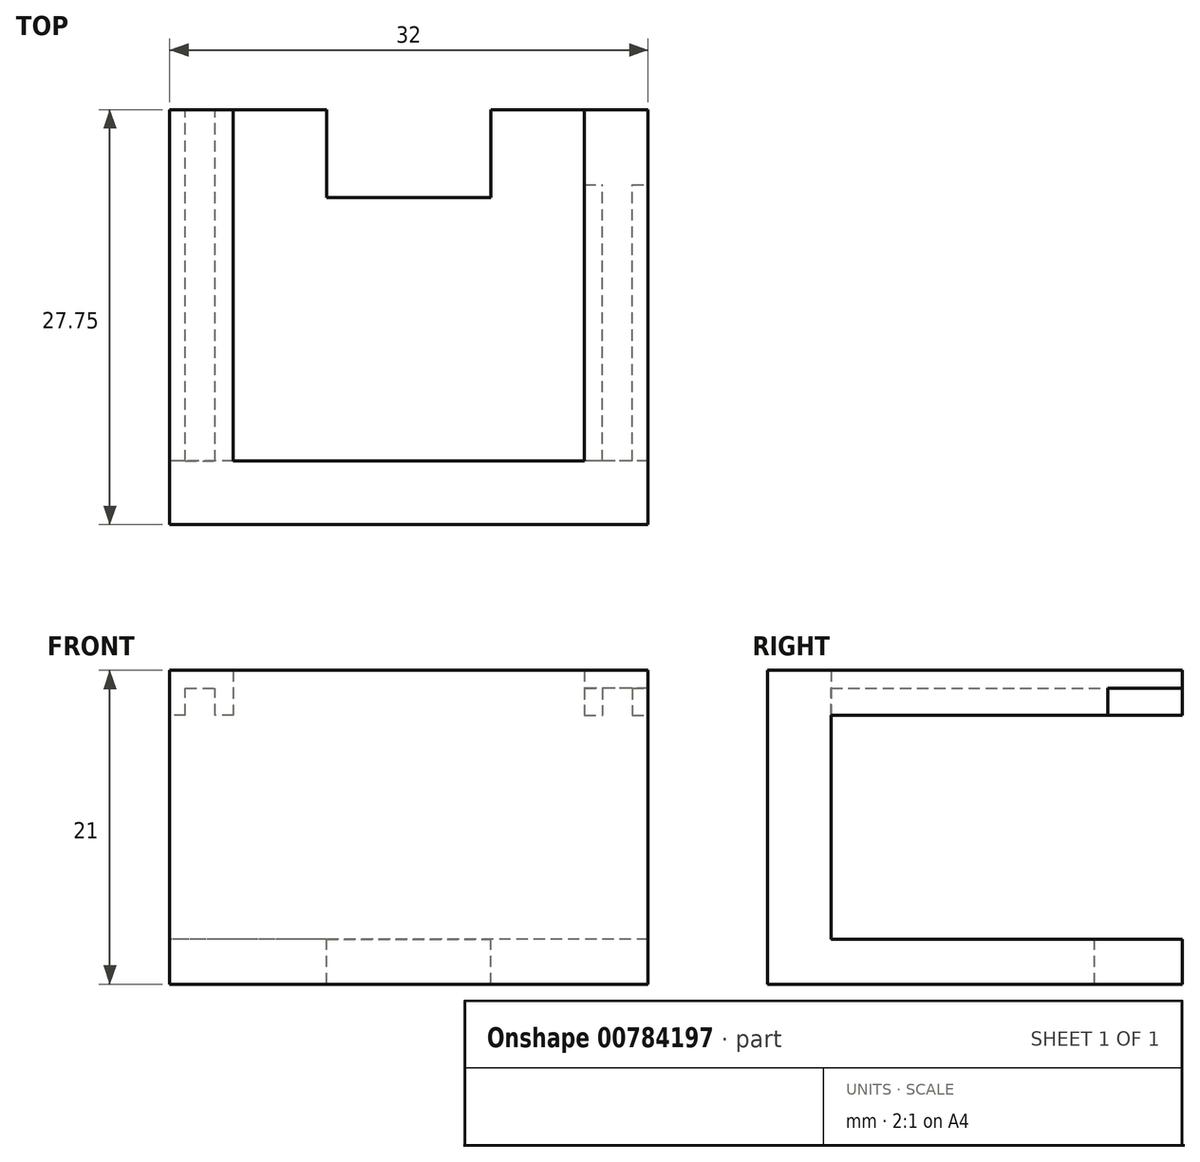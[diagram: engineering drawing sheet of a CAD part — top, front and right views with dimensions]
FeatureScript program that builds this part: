
annotation { "Feature Type Name" : "Feature", "Feature Type Description" : "" }
export const myFeature = defineFeature(function(context is Context, id is Id, definition is map)
    precondition{}
    {
        {
            var Q0;
            Q0=qCreatedBy(makeId("Top.planeOp"),FACE);
            var sketch = newSketch(context, id + "F0", { "sketchPlane" : qUnion([Q0])});
            skLineSegment(sketch, "E0.bottom", {"start": v(11.75, -11.75) * mm, "end": v(-11.75, -11.75) * mm});
            skLineSegment(sketch, "E0.left", {"start": v(11.75, -11.75) * mm, "end": v(11.75, 11.75) * mm});
            skLineSegment(sketch, "E0.right", {"start": v(-11.75, -11.75) * mm, "end": v(-11.75, 11.75) * mm});
            skPoint(sketch, "E0.middle", {"position": v(0, 0) * mm});
            skLineSegment(sketch, "E1", {"start": v(-16, 11.75) * mm, "end": v(-16, -16) * mm});
            skLineSegment(sketch, "E2", {"start": v(-16, -16) * mm, "end": v(16, -16) * mm});
            skLineSegment(sketch, "E3", {"start": v(16, -16) * mm, "end": v(16, 11.75) * mm});
            skPoint(sketch, "E4", {"position": v(0, -16) * mm});
            skLineSegment(sketch, "E5", {"start": v(-11.75, 11.75) * mm, "end": v(-16, 11.75) * mm});
            skLineSegment(sketch, "E6", {"start": v(11.75, 11.75) * mm, "end": v(16, 11.75) * mm});
            skSolve(sketch);
        }
        {
            var Q0;
            Q0 = qSketchRegion(id + "F0", true);
            extrude(context, id + "F1", {"entities" : qUnion([Q0]), "depth" : 3 * mm, "offsetDistance" : 25 * mm});
        }
        {
            var Q0;
            Q0=makeQuery(id+"F1.opExtrude","CAP_FACE",FACE,{"disambiguationData":[OSD([sQuery(id+"F0.wireOp",EDGE,"E0.bottom"),sQuery(id+"F0.wireOp",EDGE,"E0.left"),sQuery(id+"F0.wireOp",EDGE,"E0.right"),sQuery(id+"F0.wireOp",EDGE,"E1"),sQuery(id+"F0.wireOp",EDGE,"E2"),sQuery(id+"F0.wireOp",EDGE,"E3"),sQuery(id+"F0.wireOp",EDGE,"E5"),sQuery(id+"F0.wireOp",EDGE,"E6")])],"isStart":true});
            var sketch = newSketch(context, id + "F2", { "sketchPlane" : qUnion([Q0])});
            skLineSegment(sketch, "E7.bottom", {"start": v(-16, 16) * mm, "end": v(16, 16) * mm});
            skLineSegment(sketch, "E7.top", {"start": v(-16, 11.75) * mm, "end": v(16, 11.75) * mm});
            skLineSegment(sketch, "E7.left", {"start": v(-16, 16) * mm, "end": v(-16, 11.75) * mm});
            skLineSegment(sketch, "E7.right", {"start": v(16, 16) * mm, "end": v(16, 11.75) * mm});
            skSolve(sketch);
        }
        {
            var Q0;
            Q0 = qSketchRegion(id + "F2", true);
            extrude(context, id + "F3", {"entities" : qUnion([Q0]), "operationType" : NewBodyOperationType.ADD, "depth" : 15 * mm, "offsetDistance" : 25 * mm});
        }
        {
            var Q0;
            Q0=makeQuery(id+"F3.boolean.opBoolean","MERGE",FACE,{"derivedFrom":[makeQuery(id+"F1.opExtrude","SWEPT_FACE",FACE,{"disambiguationData":[OSD([sQuery(id+"F0.wireOp",EDGE,"E2")])]}),makeQuery(id+"F3.opExtrude","SWEPT_FACE",FACE,{"disambiguationData":[OSD([sQuery(id+"F2.wireOp",EDGE,"E7.bottom")])]})]});
            var sketch = newSketch(context, id + "F4", { "sketchPlane" : qUnion([Q0])});
            skLineSegment(sketch, "E8.bottom", {"start": v(-16, -15) * mm, "end": v(16, -15) * mm});
            skLineSegment(sketch, "E8.top", {"start": v(-16, -18) * mm, "end": v(16, -18) * mm});
            skLineSegment(sketch, "E8.left", {"start": v(-16, -15) * mm, "end": v(-16, -18) * mm});
            skLineSegment(sketch, "E8.right", {"start": v(16, -15) * mm, "end": v(16, -18) * mm});
            skSolve(sketch);
        }
        {
            var Q0;
            Q0 = qSketchRegion(id + "F4", true);
            var Q1;
            Q1=makeQuery(id+"F1.opExtrude","SWEPT_FACE",FACE,{"disambiguationData":[OSD([sQuery(id+"F0.wireOp",EDGE,"E5")])]});
            extrude(context, id + "F5", {"entities" : qUnion([Q0]), "operationType" : NewBodyOperationType.ADD, "endBound" : BoundingType.UP_TO_SURFACE, "oppositeDirection" : true, "depth" : 25 * mm, "endBoundEntityFace" : qUnion([Q1]), "offsetDistance" : 25 * mm});
        }
        {
            var Q0;
            Q0=makeQuery(id+"F1.opExtrude","SWEPT_FACE",FACE,{"disambiguationData":[OSD([sQuery(id+"F0.wireOp",EDGE,"E5")])]});
            var sketch = newSketch(context, id + "F6", { "sketchPlane" : qUnion([Q0])});
            skLineSegment(sketch, "E9.bottom", {"start": v(14.95, 0) * mm, "end": v(12.95, 0) * mm});
            skLineSegment(sketch, "E9.top", {"start": v(14.95, 1.8) * mm, "end": v(12.95, 1.8) * mm});
            skLineSegment(sketch, "E9.left", {"start": v(14.95, 0) * mm, "end": v(14.95, 1.8) * mm});
            skLineSegment(sketch, "E9.right", {"start": v(12.95, 0) * mm, "end": v(12.95, 1.8) * mm});
            skLineSegment(sketch, "E10.MirrorCS", {"start": v(-12.95, 0) * mm, "end": v(-12.95, 1.8) * mm});
            skLineSegment(sketch, "E11.MirrorCS", {"start": v(-14.95, 1.8) * mm, "end": v(-12.95, 1.8) * mm});
            skLineSegment(sketch, "E12.MirrorCS", {"start": v(-14.95, 0) * mm, "end": v(-14.95, 1.8) * mm});
            skLineSegment(sketch, "E13.MirrorCS", {"start": v(-14.95, 0) * mm, "end": v(-12.95, 0) * mm});
            skSolve(sketch);
        }
        {
            var Q0;
            Q0 = qSketchRegion(id + "F6", true);
            var Q1;
            Q1=makeQuery(id+"F3.boolean.opBoolean","MERGE",FACE,{"derivedFrom":[makeQuery(id+"F1.opExtrude","SWEPT_FACE",FACE,{"disambiguationData":[OSD([sQuery(id+"F0.wireOp",EDGE,"E0.bottom")])]}),makeQuery(id+"F3.opExtrude","SWEPT_FACE",FACE,{"disambiguationData":[OSD([sQuery(id+"F2.wireOp",EDGE,"E7.top")])]})]});
            extrude(context, id + "F7", {"entities" : qUnion([Q0]), "operationType" : NewBodyOperationType.REMOVE, "endBound" : BoundingType.UP_TO_SURFACE, "oppositeDirection" : true, "depth" : 25 * mm, "endBoundEntityFace" : qUnion([Q1]), "offsetDistance" : 25 * mm});
        }
        {
            var Q0;
            Q0=makeQuery(id+"F1.opExtrude","SWEPT_FACE",FACE,{"disambiguationData":[OSD([sQuery(id+"F0.wireOp",EDGE,"E6")])]});
            var sketch = newSketch(context, id + "F8", { "sketchPlane" : qUnion([Q0])});
            skLineSegment(sketch, "E14.bottom", {"start": v(-11.75, 0) * mm, "end": v(-16, 0) * mm});
            skLineSegment(sketch, "E14.top", {"start": v(-11.75, 1.8) * mm, "end": v(-16, 1.8) * mm});
            skLineSegment(sketch, "E14.left", {"start": v(-11.75, 0) * mm, "end": v(-11.75, 1.8) * mm});
            skLineSegment(sketch, "E14.right", {"start": v(-16, 0) * mm, "end": v(-16, 1.8) * mm});
            skSolve(sketch);
        }
        {
            var Q0;
            Q0 = qSketchRegion(id + "F8", true);
            extrude(context, id + "F9", {"entities" : qUnion([Q0]), "operationType" : NewBodyOperationType.REMOVE, "oppositeDirection" : true, "depth" : 5 * mm, "offsetDistance" : 25 * mm});
        }
        {
            var Q0;
            Q0=makeQuery(id+"F5.opExtrude","SWEPT_FACE",FACE,{"disambiguationData":[OSD([sQuery(id+"F4.wireOp",EDGE,"E8.bottom")])]});
            var sketch = newSketch(context, id + "F10", { "sketchPlane" : qUnion([Q0])});
            skLineSegment(sketch, "E15.bottom", {"start": v(-5.5, 11.75) * mm, "end": v(5.5, 11.75) * mm});
            skLineSegment(sketch, "E15.top", {"start": v(-5.5, 5.87) * mm, "end": v(5.5, 5.87) * mm});
            skLineSegment(sketch, "E15.left", {"start": v(-5.5, 11.75) * mm, "end": v(-5.5, 5.87) * mm});
            skLineSegment(sketch, "E15.right", {"start": v(5.5, 11.75) * mm, "end": v(5.5, 5.87) * mm});
            skPoint(sketch, "E15.middle", {"position": v(0, 8.8) * mm});
            skSolve(sketch);
        }
        {
            var Q0;
            Q0 = qSketchRegion(id + "F10", true);
            extrude(context, id + "F11", {"entities" : qUnion([Q0]), "operationType" : NewBodyOperationType.REMOVE, "endBound" : BoundingType.UP_TO_NEXT, "oppositeDirection" : true, "depth" : 25 * mm, "offsetDistance" : 25 * mm});
        }
    });
